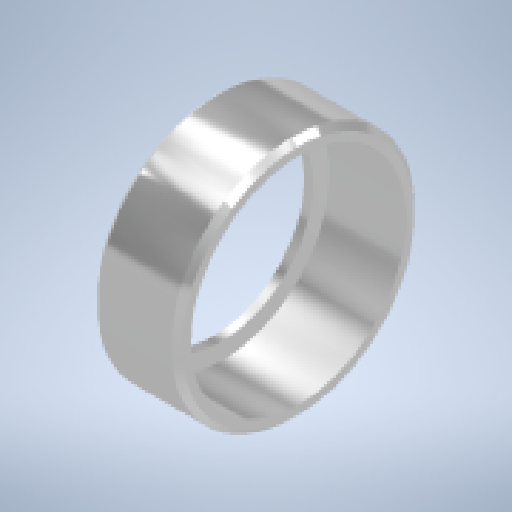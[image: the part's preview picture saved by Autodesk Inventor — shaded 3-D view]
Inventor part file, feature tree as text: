
AUTODESK INVENTOR PART (.ipt)
format: ipt  version: 2023 (Build 270158000, 158)  size: 169,472 bytes
history: native  units: mm
features: revolve x1, chamfer x1, sketch x1
ambient origin geometry x8: Origin, YZ Plane, XZ Plane, XY Plane, X Axis, Y Axis, Z Axis, Center Point
bodies: Solid1 (feature_tree)
feature tree (3):
  revolve  "Revolution1"  [1 undecoded]
  chamfer  "Chamfer1"  Distance=15.0mm
  sketch  "Sketch1"  dims[d0=38.0mm d1=2.5mm d2=15.0mm d3=1.5mm d5=90.0deg d6=32.0mm d7=1.0mm d8=2.0mm d9=45.0deg]
note: 1 required parameter value undecoded (feature->parameter linkage not recoverable at this tier; creation-order binding heuristic only, values carry confidence <= 0.55)
